# Revit family: PRD_FrankeWS_WlHngWshBsns_AnimaWashBasin_ANMX212N,216
name_source: partatom
category: Plumbing Fixtures
revit_build: Autodesk Revit 2018 (Build: 20190510_1515(x64)
units: mm (PartAtom-declared; Revit-internal decimal feet)

## family parameters
Cut with Voids When Loaded = No
Host = Face
OmniClass Number = 23.45.05.14.14
OmniClass Title = Sinks/Lavatories
Part Type = Normal
Room Calculation Point = No
Round Connector Dimension = Use Diameter
Shared = No

## types (2) — shared parameters
AssetType = Fixed
Category = Pr_40_20_96_96, Wall-hung wash basins
Color = Stainless steel
Default Elevation = 850 mm  [stored 2.78871 ft]
DiameterNominal = 15  [stored 0.0492126 ft]
DrainSize = DN 32 (1 1/4 inch.)
DurationUnit = year
Finish = Satin polish finished
FlowColdWater = 0.0 L/s
FlowHotWater = 0.0 L/s
Form = Wall hung wash basin
IfcExportAs = IfcSanitaryTerminalType
IfcExportType = WASHHANDBASIN
InletSize = DN 15 (1/2 inch.)
IntegralAccessories = Screws and plugs are not supplied.
Manufacturer = KWC Group AG
ManufacturerName = KWC Group AG
ManufacturerURL = www.kwc.com
Material = Stainless steel
MaterialsBody = Stainless steel 1.4301
MaterialsFinishAndColour = Stainless steel
NBSDescription = Wall hung wash basins
NBSReference = 45-35-70/369
NumberOfTapHoles = 1
OutletSize = DN 32 (1 1/4 inch.)
Overflow = no
ProductInformation = https://pim.kwc.com
Splashback = yes
TapMaterial = PRD_AR_StainlessSteel_SatinFinished
TypeOfBasin = Vanity basin
URL = www.kwc.com
Uniclass2015Code = Pr_40_20_96_96
Uniclass2015Title = Wall-hung wash basins
Uniclass2015Version = Products v1.10
Version = 1
WarrantyDurationUnit = year
WashHandBasinMounting = WallHung
WashHandBasinType = HandRinse
WashbasinMaterial = PRD_AR_StainlessSteel_SatinFinished
WasteKitIncluded = yes
WasteSize = 32  [stored 0.104987 ft]
WaterSupplyOverflowAndWasteHolesOverflow = None
WaterSupplyOverflowAndWasteHolesWaste = CENTRE-CENTRE
WaterSupplyOverflowAndWasteHolesWaterSupply = 32 mm  [stored 0.104987 ft]

## per-type parameters (varying)
| type | BIMObjectName | Description | Features | GrossWeight | InletDepth | InletOffset | ModelNumber | Name | NetWeight | NominalHeight | NominalLength | NominalWidth | OutletDepth | OutletOffset | Size | TapHolePosition |
| ANMX216 | PRD_AR_WallHungWashBasins_AnimaWashBasin_ANMX216 | Knee operated wash hand basin is manufactured from stainless steel - satin polish finish, material thickness 0.9 mm. Supplied complete with water spout positioned in rear right hand corner and 32 mm waste outlet. Note: The pre-mixing valve and the pipework linking the water spout to the knee operated front panel is all supplied with the washbasin. Wall mounted by fitting a top joggle strip under the upstand return and by screw fixing through the integral rear brackets. Screws and plugs are not supplied. | Wash basin with knee operations, stainless steel, 0.90 mm, satin finished, wall mounting, 305x501x268 mm (WxHxD) | 4.30 kg | 170 mm | 129 mm | 2000101028 | ANIMA Wash basins ANMX216 | 4.00 kg | 501 mm  [stored 1.6437 ft] | 268 mm | 501 mm  [stored 1.6437 ft] | 126 mm | 134 mm | 305 x 501 x 268 mm | right |
| ANMX212N | PRD_AR_WallHungWashBasins_AnimaWashBasin_ANMX212N | Knee operated wash hand basin is manufactured from stainless steel - satin polish finish, material thickness 0.9mm. Supplied complete with water spout positioned in rear right hand corner and 32mm waste outlet. Note: The pre-mixing valve and the pipework linking the water spout to the knee operated front panel is all supplied with the washbasin. Wall mounted by fitting a top joggle strip under the upstand return and by screw fixing through the integral rear brackets. Screws and plugs are not supplied. | Wash basin with knee operations, stainless steel, 0.90 mm, satin polish finished, wall mounting | 5.30 kg | 198 mm  [stored 0.649606 ft] | 162 mm  [stored 0.531496 ft] | 2030034760 | ANIMA Wash basins ANMX212N | 5.00 kg | 535 mm  [stored 1.75525 ft] | 343 mm  [stored 1.12533 ft] | 338 mm  [stored 1.10892 ft] | 161 mm | 171 mm | 338 x 535 x 343 mm | Right |

note: column(s) folded — value = type name in every type: Model, ModelReference, Type

note: [stored X ft] marks values corroborated as IEEE doubles in the binary element streams (Revit-internal decimal feet)

## geometry (parser evidence)
native form markers: Sweep x8
no freeform markers — native parametric forms only
